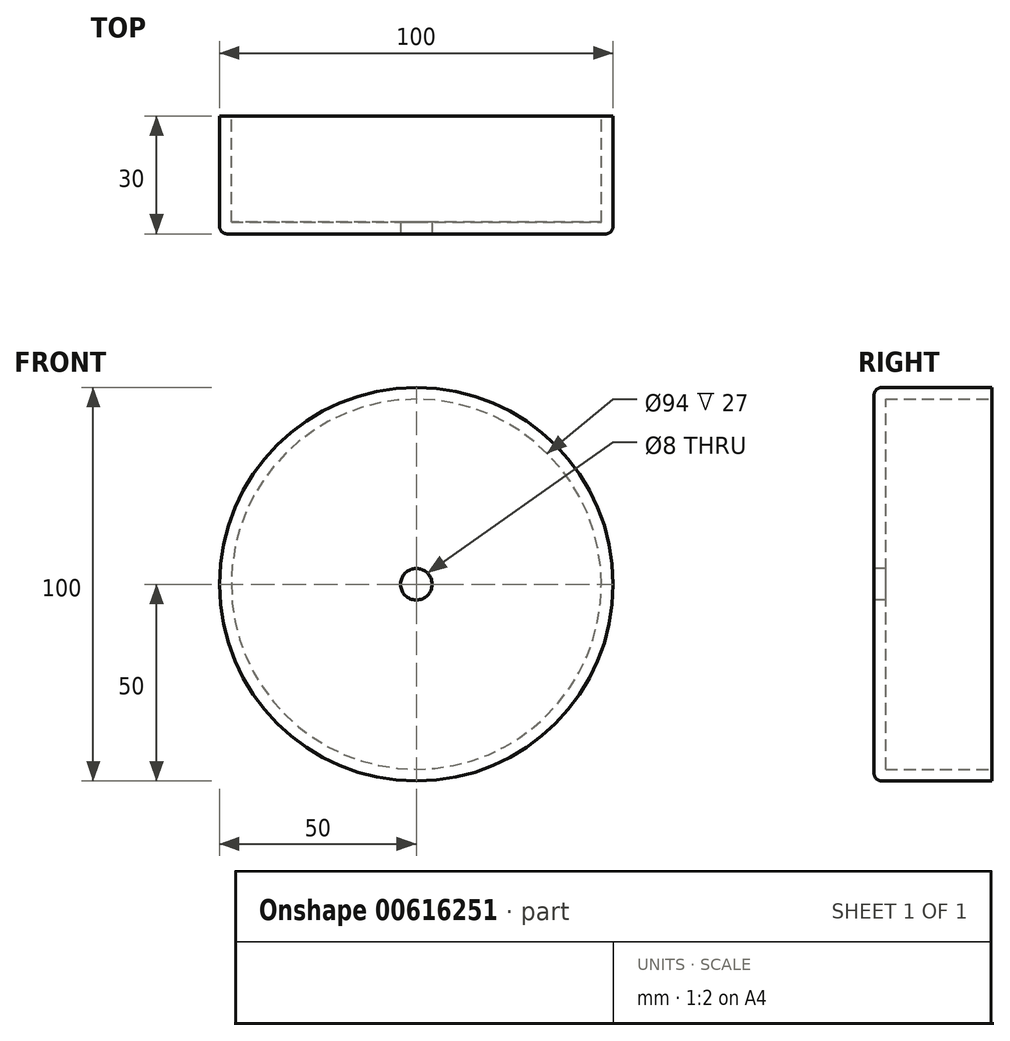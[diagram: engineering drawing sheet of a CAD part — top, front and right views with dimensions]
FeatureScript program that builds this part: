
annotation { "Feature Type Name" : "Feature", "Feature Type Description" : "" }
export const myFeature = defineFeature(function(context is Context, id is Id, definition is map)
    precondition{}
    {
        {
            var Q0;
            Q0=qCreatedBy(makeId("Front.planeOp"),FACE);
            var sketch = newSketch(context, id + "F0", { "sketchPlane" : qUnion([Q0])});
            skCircle(sketch, "E0", {"center": v(0, 0) * mm, "radius": 50 * mm});
            skSolve(sketch);
        }
        {
            var Q0;
            Q0=qSketchRegion(id+"F0",true);
            extrude(context, id + "F1", {"entities" : qUnion([Q0]), "depth" : 30 * mm});
        }
        {
            var Q0;
            Q0=makeQuery(id+"F1.opExtrude","CAP_FACE",FACE,{"disambiguationData":[OSD([sQuery(id+"F0.wireOp",EDGE,"E0")])],"isStart":true});
            shell(context, id + "F2", {"entities" : qUnion([Q0]), "thickness" : 3 * mm});
        }
        {
            var Q0;
            Q0=makeQuery(id+"F1.opExtrude","CAP_EDGE",EDGE,{"disambiguationData":[OSD([sQuery(id+"F0.wireOp",EDGE,"E0")])],"isStart":false});
            fillet(context, id + "F3", {"entities" : qUnion([Q0]), "radius" : 2 * mm, "tangentPropagation" : true, "allowEdgeOverflow" : false});
        }
        {
            var Q0;
            Q0=makeQuery(id+"F1.opExtrude","CAP_FACE",FACE,{"disambiguationData":[OSD([sQuery(id+"F0.wireOp",EDGE,"E0")])],"isStart":false});
            var sketch = newSketch(context, id + "F4", { "sketchPlane" : qUnion([Q0])});
            skPoint(sketch, "E1", {"position": v(0, 0) * mm});
            skSolve(sketch);
        }
        {
            var Q0;
            Q0=sQuery(id+"F4.wireOp",VERTEX,"E1");
            var Q1;
            Q1=makeQuery(id+"F1.opExtrude","SWEPT_BODY",BODY,{"disambiguationData":[OSD([sQuery(id+"F0.wireOp",EDGE,"E0")])]});
            hole(context, id + "F5", {"style" : HoleStyle.SIMPLE, "endStyle" : HoleEndStyle.THROUGH, "holeDiameter" : 8 * mm, "locations" : qUnion([Q0]), "scope" : qUnion([Q1]), "majorDiameter" : 5 * mm, "tappedDepth" : 12 * mm, "tapClearance" : 3});
        }
    });
